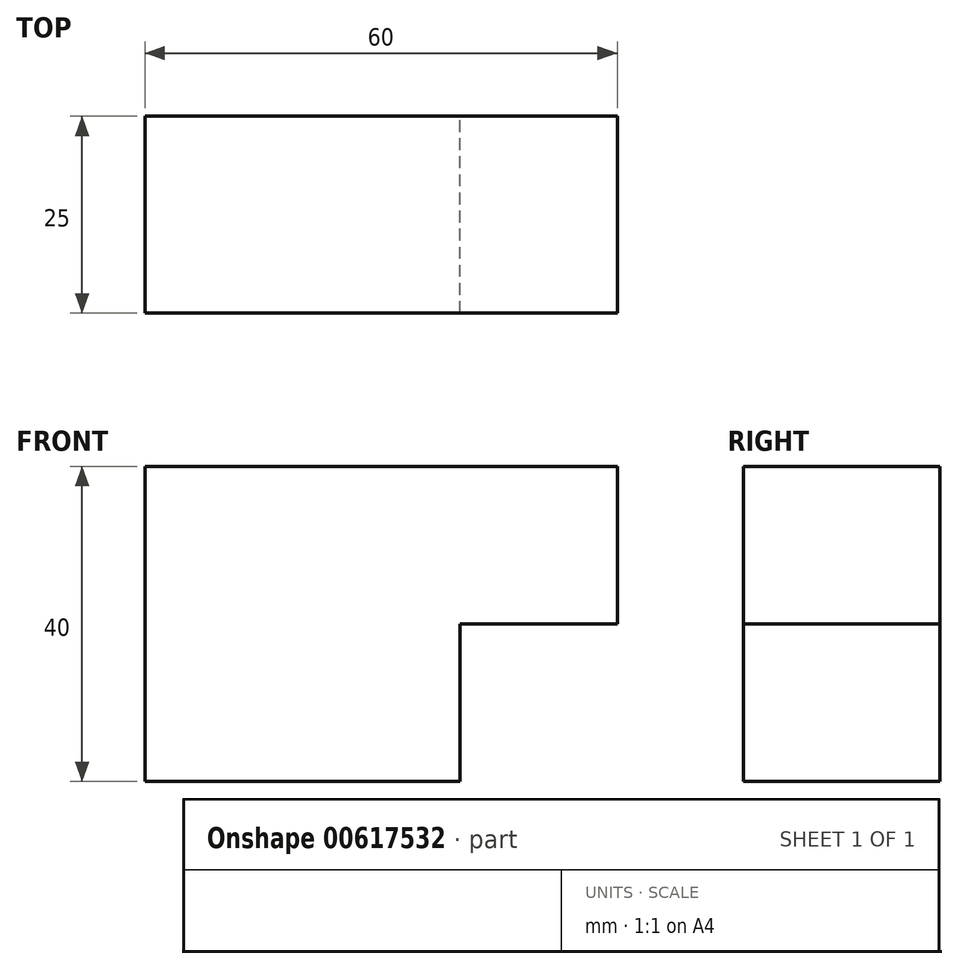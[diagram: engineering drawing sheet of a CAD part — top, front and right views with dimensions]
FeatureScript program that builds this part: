
annotation { "Feature Type Name" : "Feature", "Feature Type Description" : "" }
export const myFeature = defineFeature(function(context is Context, id is Id, definition is map)
    precondition{}
    {
        {
            var Q0;
            Q0=qCreatedBy(makeId("Front.planeOp"),FACE);
            var sketch = newSketch(context, id + "F0", { "sketchPlane" : qUnion([Q0])});
            skLineSegment(sketch, "E0", {"start": v(0, 0) * mm, "end": v(0, -20) * mm});
            skLineSegment(sketch, "E1", {"start": v(0, -20) * mm, "end": v(0, 20) * mm});
            skLineSegment(sketch, "E2", {"start": v(0, 20) * mm, "end": v(20, 20) * mm});
            skLineSegment(sketch, "E3", {"start": v(20, 20) * mm, "end": v(40, 20) * mm});
            skLineSegment(sketch, "E4", {"start": v(40, 20) * mm, "end": v(60, 20) * mm});
            skLineSegment(sketch, "E5", {"start": v(60, 20) * mm, "end": v(60, 0) * mm});
            skLineSegment(sketch, "E6", {"start": v(60, 0) * mm, "end": v(40, 0) * mm});
            skLineSegment(sketch, "E7", {"start": v(40, 0) * mm, "end": v(40, 20) * mm});
            skLineSegment(sketch, "E8", {"start": v(20, 20) * mm, "end": v(20, 0) * mm});
            skLineSegment(sketch, "E9", {"start": v(20, 0) * mm, "end": v(0, 0) * mm});
            skLineSegment(sketch, "E10", {"start": v(20, -20) * mm, "end": v(20, 0) * mm});
            skLineSegment(sketch, "E11", {"start": v(20, -20) * mm, "end": v(0, -20) * mm});
            skLineSegment(sketch, "E12", {"start": v(20, -20) * mm, "end": v(40, -20) * mm});
            skLineSegment(sketch, "E13", {"start": v(40, -20) * mm, "end": v(40, 0) * mm});
            skSolve(sketch);
        }
        {
            var Q0;
            Q0 = qSketchRegion(id + "F0", true);
            extrude(context, id + "F1", {"entities" : qUnion([Q0]), "depth" : 25 * mm, "offsetDistance" : 25 * mm});
        }
    });
